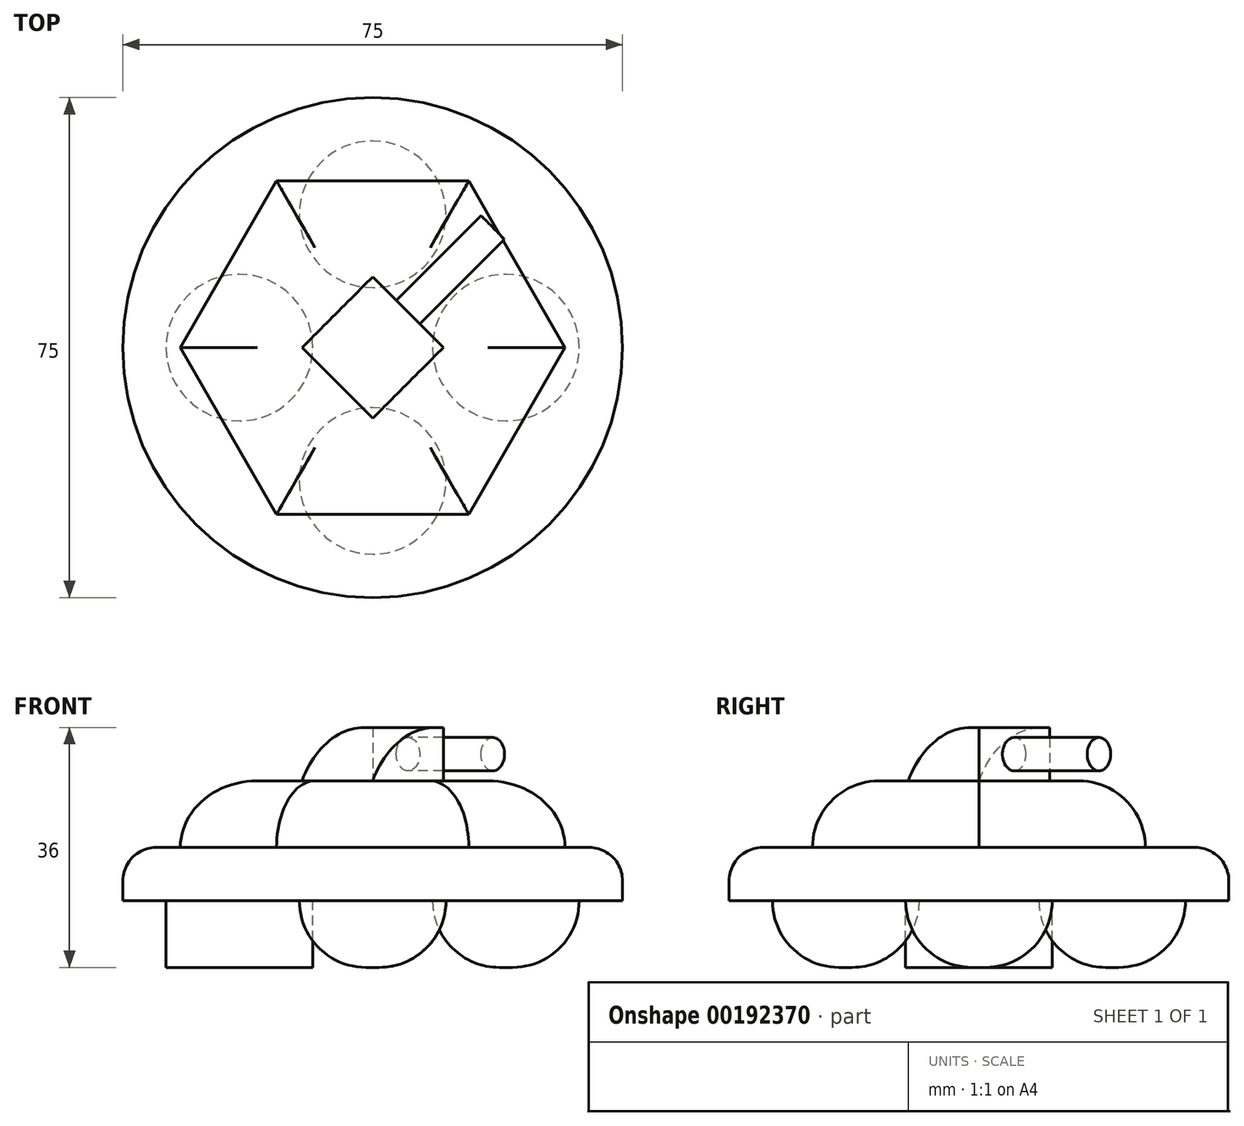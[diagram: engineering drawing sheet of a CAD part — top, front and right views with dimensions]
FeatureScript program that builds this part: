
annotation { "Feature Type Name" : "Feature", "Feature Type Description" : "" }
export const myFeature = defineFeature(function(context is Context, id is Id, definition is map)
    precondition{}
    {
        {
            var Q0;
            Q0=qCreatedBy(makeId("Top.planeOp"),FACE);
            var sketch = newSketch(context, id + "F0", { "sketchPlane" : qUnion([Q0])});
            skCircle(sketch, "E0", {"center": v(0, 0) * mm, "radius": 37.5 * mm});
            skSolve(sketch);
        }
        {
            var Q0;
            Q0=makeQuery(id+"F0.imprint","IMPRINT",FACE,{"disambiguationData":[TD([[makeQuery(id+"F0.imprint","IMPRINT",EDGE,{"derivedFrom":sQuery(id+"F0.wireOp",EDGE,"E0")}),1.0]])]});
            extrude(context, id + "F1", {"entities" : qUnion([Q0]), "depth" : 8 * mm});
        }
        {
            var Q0;
            Q0=makeQuery(id+"F1.opExtrude","CAP_EDGE",EDGE,{"disambiguationData":[OSD([sQuery(id+"F0.wireOp",EDGE,"E0")])],"isStart":false});
            fillet(context, id + "F2", {"entities" : qUnion([Q0]), "radius" : 5 * mm, "tangentPropagation" : true, "allowEdgeOverflow" : false});
        }
        {
            var Q0;
            Q0=makeQuery(id+"F1.opExtrude","CAP_FACE",FACE,{"disambiguationData":[OSD([sQuery(id+"F0.wireOp",EDGE,"E0")])],"isStart":true});
            var sketch = newSketch(context, id + "F3", { "sketchPlane" : qUnion([Q0])});
            skCircle(sketch, "E1", {"center": v(20, 0) * mm, "radius": 11 * mm});
            skCircle(sketch, "E2.MirrorC", {"center": v(-20, 0) * mm, "radius": 11 * mm});
            skCircle(sketch, "E3", {"center": v(0, 20) * mm, "radius": 11 * mm});
            skCircle(sketch, "E4.MirrorC", {"center": v(0, -20) * mm, "radius": 11 * mm});
            skSolve(sketch);
        }
        {
            var Q0;
            Q0 = qSketchRegion(id + "F3", true);
            extrude(context, id + "F4", {"entities" : qUnion([Q0]), "operationType" : NewBodyOperationType.ADD, "depth" : 10 * mm});
        }
        {
            var Q0;
            Q0=makeQuery(id+"F4.opExtrude","CAP_FACE",FACE,{"disambiguationData":[OSD([sQuery(id+"F3.wireOp",EDGE,"E4.MirrorC")])],"isStart":false});
            var Q1;
            Q1=makeQuery(id+"F4.opExtrude","CAP_FACE",FACE,{"disambiguationData":[OSD([sQuery(id+"F3.wireOp",EDGE,"E2.MirrorC")])],"isStart":false});
            var Q2;
            Q2=makeQuery(id+"F4.opExtrude","CAP_FACE",FACE,{"disambiguationData":[OSD([sQuery(id+"F3.wireOp",EDGE,"E3")])],"isStart":false});
            var Q3;
            Q3=makeQuery(id+"F4.opExtrude","CAP_FACE",FACE,{"disambiguationData":[OSD([sQuery(id+"F3.wireOp",EDGE,"E1")])],"isStart":false});
            fillet(context, id + "F5", {"entities" : qUnion([Q0, Q1, Q2, Q3]), "radius" : 10 * mm, "tangentPropagation" : true, "allowEdgeOverflow" : false});
        }
        {
            var Q0;
            Q0=makeQuery(id+"F1.opExtrude","CAP_FACE",FACE,{"disambiguationData":[OSD([sQuery(id+"F0.wireOp",EDGE,"E0")])],"isStart":false});
            var sketch = newSketch(context, id + "F6", { "sketchPlane" : qUnion([Q0])});
            skCircle(sketch, "E5.cCircle", {"center": v(0, 0) * mm, "radius": 25 * mm, "construction": true});
            skLineSegment(sketch, "E5.0", {"start": v(28.87, 0) * mm, "end": v(14.43, -25) * mm});
            skLineSegment(sketch, "E5.1", {"start": v(14.43, -25) * mm, "end": v(-14.43, -25) * mm});
            skLineSegment(sketch, "E5.2", {"start": v(-14.43, -25) * mm, "end": v(-28.87, 0) * mm});
            skLineSegment(sketch, "E5.3", {"start": v(-28.87, 0) * mm, "end": v(-14.43, 25) * mm});
            skLineSegment(sketch, "E5.4", {"start": v(-14.43, 25) * mm, "end": v(14.43, 25) * mm});
            skLineSegment(sketch, "E5.5", {"start": v(14.43, 25) * mm, "end": v(28.87, 0) * mm});
            skPoint(sketch, "E5.0.midPoint", {"position": v(21.65, -12.5) * mm});
            skSolve(sketch);
        }
        {
            var Q0;
            Q0 = qSketchRegion(id + "F6", true);
            extrude(context, id + "F7", {"entities" : qUnion([Q0]), "operationType" : NewBodyOperationType.ADD, "depth" : 10 * mm});
        }
        {
            var Q0;
            Q0=makeQuery(id+"F7.opExtrude","CAP_FACE",FACE,{"disambiguationData":[OSD([sQuery(id+"F6.wireOp",EDGE,"E5.0"),sQuery(id+"F6.wireOp",EDGE,"E5.1"),sQuery(id+"F6.wireOp",EDGE,"E5.2"),sQuery(id+"F6.wireOp",EDGE,"E5.3"),sQuery(id+"F6.wireOp",EDGE,"E5.4"),sQuery(id+"F6.wireOp",EDGE,"E5.5")])],"isStart":false});
            fillet(context, id + "F8", {"entities" : qUnion([Q0]), "radius" : 10 * mm, "tangentPropagation" : true, "allowEdgeOverflow" : false});
        }
        {
            var Q0;
            Q0=makeQuery(id+"F1.opExtrude","CAP_FACE",FACE,{"disambiguationData":[OSD([sQuery(id+"F0.wireOp",EDGE,"E0")])],"isStart":false});
            var sketch = newSketch(context, id + "F9", { "sketchPlane" : qUnion([Q0])});
            skCircle(sketch, "E6.cCircle", {"center": v(0, 0) * mm, "radius": 7.5 * mm, "construction": true});
            skLineSegment(sketch, "E6.0", {"start": v(0, 10.6) * mm, "end": v(10.6, 0) * mm});
            skLineSegment(sketch, "E6.1", {"start": v(10.6, 0) * mm, "end": v(0, -10.6) * mm});
            skLineSegment(sketch, "E6.2", {"start": v(0, -10.6) * mm, "end": v(-10.6, 0) * mm});
            skLineSegment(sketch, "E6.3", {"start": v(-10.6, 0) * mm, "end": v(0, 10.6) * mm});
            skPoint(sketch, "E6.0.midPoint", {"position": v(5.3, 5.3) * mm});
            skSolve(sketch);
        }
        {
            var Q0;
            Q0 = qSketchRegion(id + "F9", true);
            extrude(context, id + "F10", {"entities" : qUnion([Q0]), "operationType" : NewBodyOperationType.ADD, "depth" : 18 * mm});
        }
        {
            var Q0;
            Q0=makeQuery(id+"F10.opExtrude","CAP_EDGE",EDGE,{"disambiguationData":[OSD([sQuery(id+"F9.wireOp",EDGE,"E6.2")])],"isStart":false});
            fillet(context, id + "F11", {"entities" : qUnion([Q0]), "radius" : 15 * mm, "tangentPropagation" : true, "allowEdgeOverflow" : false});
        }
        {
            var Q0;
            Q0=makeQuery(id+"F10.opExtrude","SWEPT_FACE",FACE,{"disambiguationData":[OSD([sQuery(id+"F9.wireOp",EDGE,"E6.0")])]});
            var sketch = newSketch(context, id + "F12", { "sketchPlane" : qUnion([Q0])});
            skCircle(sketch, "E7", {"center": v(0, 22) * mm, "radius": 2.5 * mm});
            skPoint(sketch, "E7.centerSnap0", {"position": v(7.5, 22) * mm});
            skSolve(sketch);
        }
        {
            var Q0;
            Q0 = qSketchRegion(id + "F12", true);
            extrude(context, id + "F13", {"entities" : qUnion([Q0]), "operationType" : NewBodyOperationType.ADD, "depth" : 18 * mm});
        }
    });
